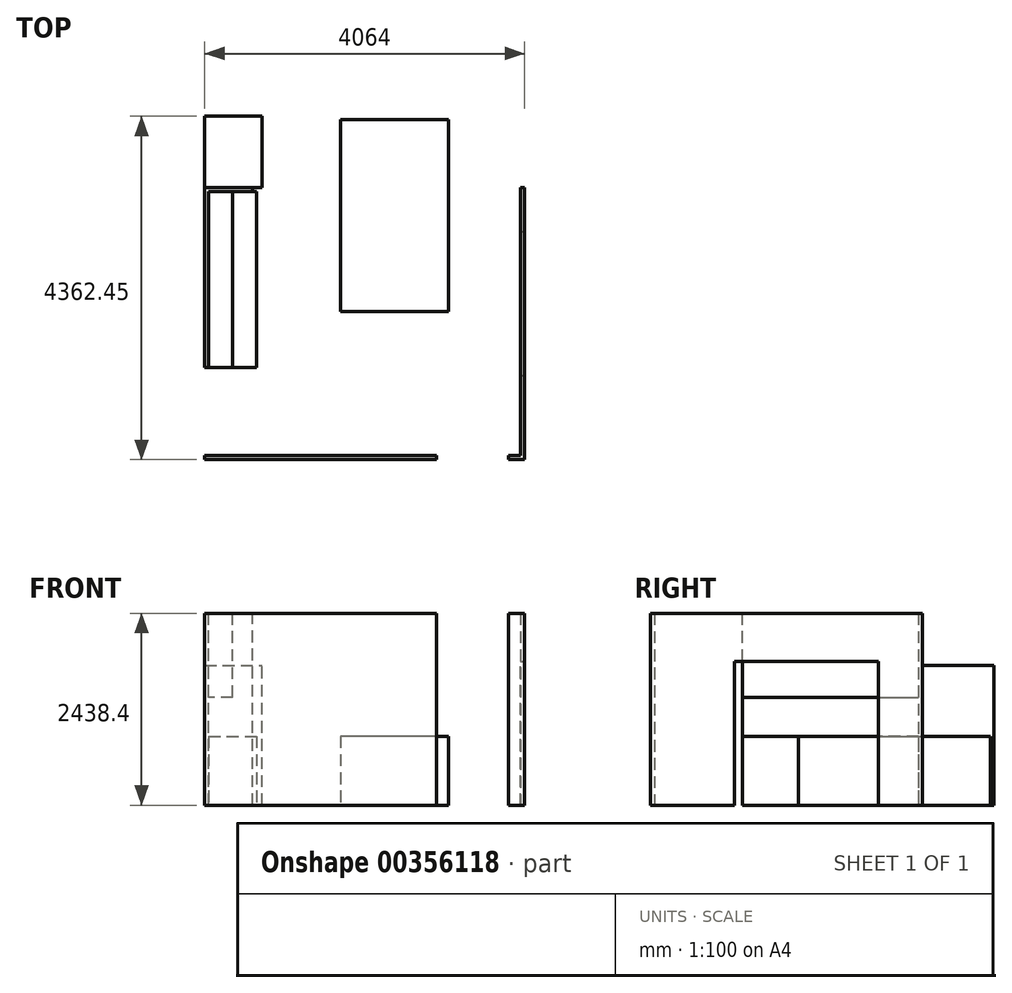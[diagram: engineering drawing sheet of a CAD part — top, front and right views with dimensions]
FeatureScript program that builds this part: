
annotation { "Feature Type Name" : "Feature", "Feature Type Description" : "" }
export const myFeature = defineFeature(function(context is Context, id is Id, definition is map)
    precondition{}
    {
        {
            var Q0;
            Q0=qCreatedBy(makeId("Top.planeOp"),FACE);
            var sketch = newSketch(context, id + "F0", { "sketchPlane" : qUnion([Q0])});
            skLineSegment(sketch, "E0.bottom", {"start": v(-1981.2, 1676.4) * mm, "end": v(1981.2, 1676.4) * mm});
            skLineSegment(sketch, "E0.top", {"start": v(-1981.2, -1676.4) * mm, "end": v(1981.2, -1676.4) * mm});
            skLineSegment(sketch, "E0.left", {"start": v(-1981.2, 1676.4) * mm, "end": v(-1981.2, -1676.4) * mm});
            skLineSegment(sketch, "E0.right", {"start": v(1981.2, 1676.4) * mm, "end": v(1981.2, -1676.4) * mm});
            skPoint(sketch, "E0.middle", {"position": v(0, 0) * mm});
            skLineSegment(sketch, "E1.0", {"start": v(-2032, 1727.2) * mm, "end": v(2032, 1727.2) * mm});
            skLineSegment(sketch, "E1.1", {"start": v(-2032, 1727.2) * mm, "end": v(-2032, -1727.2) * mm});
            skLineSegment(sketch, "E1.2", {"start": v(-2032, -1727.2) * mm, "end": v(2032, -1727.2) * mm});
            skLineSegment(sketch, "E1.3", {"start": v(2032, 1727.2) * mm, "end": v(2032, -1727.2) * mm});
            skSolve(sketch);
        }
        {
            var Q0;
            Q0=makeQuery(id+"F0.imprint","IMPRINT",FACE,{"disambiguationData":[TD([[makeQuery(id+"F0.imprint","IMPRINT",EDGE,{"derivedFrom":sQuery(id+"F0.wireOp",EDGE,"E0.bottom")}),1.0]])]});
            extrude(context, id + "F1", {"entities" : qUnion([Q0]), "depth" : 2438.4 * mm});
        }
        {
            var Q0;
            Q0=makeQuery(id+"F1.opExtrude","SWEPT_FACE",FACE,{"disambiguationData":[OSD([sQuery(id+"F0.wireOp",EDGE,"E1.1")])]});
            var sketch = newSketch(context, id + "F2", { "sketchPlane" : qUnion([Q0])});
            skLineSegment(sketch, "E2.bottom", {"start": v(1727.2, 0) * mm, "end": v(558.8, 0) * mm});
            skLineSegment(sketch, "E2.top", {"start": v(1625.6, 2438.4) * mm, "end": v(558.8, 2438.4) * mm});
            skLineSegment(sketch, "E2.left", {"start": v(1676.4, 0) * mm, "end": v(1676.4, 2438.4) * mm});
            skLineSegment(sketch, "E2.right", {"start": v(558.8, 0) * mm, "end": v(558.8, 2438.4) * mm});
            skSolve(sketch);
        }
        {
            var Q0;
            {var subQ2=sQuery(id+"F2.wireOp",EDGE,"E2.top");Q0=makeQuery(id+"F2.imprint","IMPRINT",FACE,{"disambiguationData":[TD([[makeQuery(id+"F2.imprint","IMPRINT",EDGE,{"derivedFrom":subQ2}),-1.0]])]});}
            extrude(context, id + "F3", {"entities" : qUnion([Q0]), "operationType" : NewBodyOperationType.REMOVE, "oppositeDirection" : true, "depth" : 50.8 * mm});
        }
        {
            var Q0;
            Q0=makeQuery(id+"F1.opExtrude","SWEPT_FACE",FACE,{"disambiguationData":[OSD([sQuery(id+"F0.wireOp",EDGE,"E1.0")])]});
            var sketch = newSketch(context, id + "F4", { "sketchPlane" : qUnion([Q0])});
            skLineSegment(sketch, "E3.bottom", {"start": v(-1981.2, 0) * mm, "end": v(-914.4, 0) * mm});
            skLineSegment(sketch, "E3.top", {"start": v(-1981.2, 2438.4) * mm, "end": v(-914.4, 2438.4) * mm});
            skLineSegment(sketch, "E3.left", {"start": v(-1981.2, 0) * mm, "end": v(-1981.2, 2438.4) * mm});
            skLineSegment(sketch, "E3.right", {"start": v(-914.4, 0) * mm, "end": v(-914.4, 2438.4) * mm});
            skSolve(sketch);
        }
        {
            var Q0;
            Q0=makeQuery(id+"F4.imprint","IMPRINT",FACE,{"disambiguationData":[TD([[makeQuery(id+"F4.imprint","IMPRINT",EDGE,{"derivedFrom":sQuery(id+"F4.wireOp",EDGE,"E3.bottom")}),-1.0]])]});
            extrude(context, id + "F5", {"entities" : qUnion([Q0]), "operationType" : NewBodyOperationType.REMOVE, "oppositeDirection" : true, "depth" : 50.8 * mm});
        }
        {
            var Q0;
            Q0=makeQuery(id+"F3.boolean.opBoolean","MERGE",FACE,{"derivedFrom":[makeQuery(id+"F1.opExtrude","SWEPT_FACE",FACE,{"disambiguationData":[OSD([sQuery(id+"F0.wireOp",EDGE,"E0.top")])]}),makeQuery(id+"F3.opExtrude","SWEPT_FACE",FACE,{"disambiguationData":[OSD([sQuery(id+"F2.wireOp",EDGE,"E2.left")])]})]});
            var sketch = newSketch(context, id + "F6", { "sketchPlane" : qUnion([Q0])});
            skLineSegment(sketch, "E4.bottom", {"start": v(-1828.8, 0) * mm, "end": v(-914.4, 0) * mm});
            skLineSegment(sketch, "E4.top", {"start": v(-1828.8, 2438.4) * mm, "end": v(-914.4, 2438.4) * mm});
            skLineSegment(sketch, "E4.left", {"start": v(-1828.8, 0) * mm, "end": v(-1828.8, 2438.4) * mm});
            skLineSegment(sketch, "E4.right", {"start": v(-914.4, 0) * mm, "end": v(-914.4, 2438.4) * mm});
            skSolve(sketch);
        }
        {
            var Q0;
            Q0=makeQuery(id+"F6.imprint","IMPRINT",FACE,{"disambiguationData":[TD([[makeQuery(id+"F6.imprint","IMPRINT",EDGE,{"derivedFrom":sQuery(id+"F6.wireOp",EDGE,"E4.bottom")}),-1.0]])]});
            extrude(context, id + "F7", {"entities" : qUnion([Q0]), "operationType" : NewBodyOperationType.REMOVE, "oppositeDirection" : true, "depth" : 50.8 * mm});
        }
        {
            var Q0;
            Q0=makeQuery(id+"F1.opExtrude","SWEPT_FACE",FACE,{"disambiguationData":[OSD([sQuery(id+"F0.wireOp",EDGE,"E1.3")])]});
            var sketch = newSketch(context, id + "F8", { "sketchPlane" : qUnion([Q0])});
            skLineSegment(sketch, "E5.bottom", {"start": v(-660.4, 0) * mm, "end": v(1168.4, 0) * mm});
            skLineSegment(sketch, "E5.top", {"start": v(-660.4, 1828.8) * mm, "end": v(1168.4, 1828.8) * mm});
            skLineSegment(sketch, "E5.left", {"start": v(-660.4, 0) * mm, "end": v(-660.4, 1828.8) * mm});
            skLineSegment(sketch, "E5.right", {"start": v(1168.4, 0) * mm, "end": v(1168.4, 1828.8) * mm});
            skSolve(sketch);
        }
        {
            var Q0;
            Q0=makeQuery(id+"F8.imprint","IMPRINT",FACE,{"disambiguationData":[TD([[makeQuery(id+"F8.imprint","IMPRINT",EDGE,{"derivedFrom":sQuery(id+"F8.wireOp",EDGE,"E5.bottom")}),-1.0]])]});
            extrude(context, id + "F9", {"entities" : qUnion([Q0]), "operationType" : NewBodyOperationType.REMOVE, "oppositeDirection" : true, "depth" : 50.8 * mm});
        }
        {
            var Q0;
            Q0=makeQuery(id+"F1.opExtrude","SWEPT_FACE",FACE,{"disambiguationData":[OSD([sQuery(id+"F0.wireOp",EDGE,"E0.left")])]});
            var sketch = newSketch(context, id + "F10", { "sketchPlane" : qUnion([Q0])});
            skLineSegment(sketch, "E6.bottom", {"start": v(-558.8, 2438.4) * mm, "end": v(1727.2, 2438.4) * mm});
            skLineSegment(sketch, "E6.top", {"start": v(-558.8, 1371.6) * mm, "end": v(1727.2, 1371.6) * mm});
            skLineSegment(sketch, "E6.left", {"start": v(-558.8, 2438.4) * mm, "end": v(-558.8, 1371.6) * mm});
            skLineSegment(sketch, "E6.right", {"start": v(1727.2, 2438.4) * mm, "end": v(1727.2, 1371.6) * mm});
            skSolve(sketch);
        }
        {
            var Q0;
            {var subQ0=sQuery(id+"F0.wireOp",EDGE,"E1.1");var subQ1=sQuery(id+"F0.wireOp",EDGE,"E1.0");var subQ2=sQuery(id+"F0.wireOp",EDGE,"E0.left");var subQ3=sQuery(id+"F0.wireOp",EDGE,"E0.bottom");Q0=makeQuery(id+"F5.boolean.opBoolean","SPLIT",FACE,{"disambiguationData":[TD([makeQuery(id+"F1.opExtrude","SWEPT_FACE",FACE,{"disambiguationData":[OSD([subQ3])]})])],"derivedFrom":makeQuery(id+"F1.opExtrude","CAP_FACE",FACE,{"disambiguationData":[OSD([subQ3,sQuery(id+"F0.wireOp",EDGE,"E0.top"),subQ2,sQuery(id+"F0.wireOp",EDGE,"E0.right"),subQ1,subQ0,sQuery(id+"F0.wireOp",EDGE,"E1.2"),sQuery(id+"F0.wireOp",EDGE,"E1.3")])],"isStart":true})});}
            var sketch = newSketch(context, id + "F11", { "sketchPlane" : qUnion([Q0])});
            skPoint(sketch, "E7.start.orphan", {"position": v(914.4, -1066.8) * mm});
            skLineSegment(sketch, "E8.bottom", {"start": v(-1981.2, -1676.4) * mm, "end": v(-1371.6, -1676.4) * mm});
            skLineSegment(sketch, "E8.top", {"start": v(-1981.2, 558.8) * mm, "end": v(-1371.6, 558.8) * mm});
            skLineSegment(sketch, "E8.left", {"start": v(-1981.2, -1676.4) * mm, "end": v(-1981.2, 558.8) * mm});
            skLineSegment(sketch, "E8.right", {"start": v(-1371.6, -1676.4) * mm, "end": v(-1371.6, 558.8) * mm});
            skSolve(sketch);
        }
        {
            var Q0;
            Q0=makeQuery(id+"F11.imprint","IMPRINT",FACE,{"disambiguationData":[TD([[makeQuery(id+"F11.imprint","IMPRINT",EDGE,{"derivedFrom":sQuery(id+"F11.wireOp",EDGE,"E8.bottom")}),1.0]])]});
            extrude(context, id + "F12", {"entities" : qUnion([Q0]), "oppositeDirection" : true, "depth" : 876.3 * mm});
        }
        {
            var Q0;
            {var subQ3=sQuery(id+"F10.wireOp",EDGE,"E6.left");Q0=makeQuery(id+"F10.imprint","IMPRINT",FACE,{"disambiguationData":[TD([[makeQuery(id+"F10.imprint","IMPRINT",EDGE,{"derivedFrom":subQ3}),-1.0]])]});}
            extrude(context, id + "F13", {"entities" : qUnion([Q0]), "depth" : 304.8 * mm});
        }
        {
            var Q0;
            Q0=makeQuery(id+"F1.opExtrude","SWEPT_FACE",FACE,{"disambiguationData":[OSD([sQuery(id+"F0.wireOp",EDGE,"E0.bottom")])]});
            var sketch = newSketch(context, id + "F14", { "sketchPlane" : qUnion([Q0])});
            skLineSegment(sketch, "E9.bottom", {"start": v(914.4, 0) * mm, "end": v(-1422.4, 0) * mm});
            skLineSegment(sketch, "E9.top", {"start": v(914.4, 2438.4) * mm, "end": v(-1422.4, 2438.4) * mm});
            skLineSegment(sketch, "E9.left", {"start": v(914.4, 0) * mm, "end": v(914.4, 2438.4) * mm});
            skLineSegment(sketch, "E9.right", {"start": v(-1422.4, 0) * mm, "end": v(-1422.4, 2438.4) * mm});
            skSolve(sketch);
        }
        {
            var Q0;
            Q0 = qSketchRegion(id + "F14", true);
            extrude(context, id + "F15", {"entities" : qUnion([Q0]), "operationType" : NewBodyOperationType.REMOVE, "oppositeDirection" : true, "depth" : 50.8 * mm});
        }
        {
            var Q0;
            Q0=qCreatedBy(makeId("Top.planeOp"),FACE);
            var sketch = newSketch(context, id + "F16", { "sketchPlane" : qUnion([Q0])});
            skLineSegment(sketch, "E10.bottom", {"start": v(1066.8, 152.4) * mm, "end": v(-304.8, 152.4) * mm});
            skLineSegment(sketch, "E10.top", {"start": v(1066.8, 2590.8) * mm, "end": v(-304.8, 2590.8) * mm});
            skLineSegment(sketch, "E10.left", {"start": v(1066.8, 152.4) * mm, "end": v(1066.8, 2590.8) * mm});
            skLineSegment(sketch, "E10.right", {"start": v(-304.8, 152.4) * mm, "end": v(-304.8, 2590.8) * mm});
            skSolve(sketch);
        }
        {
            var Q0;
            Q0 = qSketchRegion(id + "F16", true);
            extrude(context, id + "F17", {"entities" : qUnion([Q0]), "depth" : 876.3 * mm});
        }
        {
            var Q0;
            {var subQ2=sQuery(id+"F0.wireOp",EDGE,"E1.1");var subQ3=sQuery(id+"F0.wireOp",EDGE,"E1.0");Q0=makeQuery(id+"F5.boolean.opBoolean","SPLIT",FACE,{"disambiguationData":[TD([makeQuery(id+"F1.opExtrude","SWEPT_FACE",FACE,{"disambiguationData":[OSD([subQ2])]})])],"derivedFrom":makeQuery(id+"F1.opExtrude","SWEPT_FACE",FACE,{"disambiguationData":[OSD([subQ3])]})});}
            var sketch = newSketch(context, id + "F18", { "sketchPlane" : qUnion([Q0])});
            skLineSegment(sketch, "E11.bottom", {"start": v(2032, 0) * mm, "end": v(1304.93, 0) * mm});
            skLineSegment(sketch, "E11.top", {"start": v(2032, 1778) * mm, "end": v(1304.92, 1778) * mm});
            skLineSegment(sketch, "E11.left", {"start": v(2032, 0) * mm, "end": v(2032, 1778) * mm});
            skLineSegment(sketch, "E11.right", {"start": v(1304.93, 0) * mm, "end": v(1304.93, 1778) * mm});
            skSolve(sketch);
        }
        {
            var Q0;
            Q0 = qSketchRegion(id + "F18", true);
            extrude(context, id + "F19", {"entities" : qUnion([Q0]), "depth" : 908.05 * mm});
        }
    });
